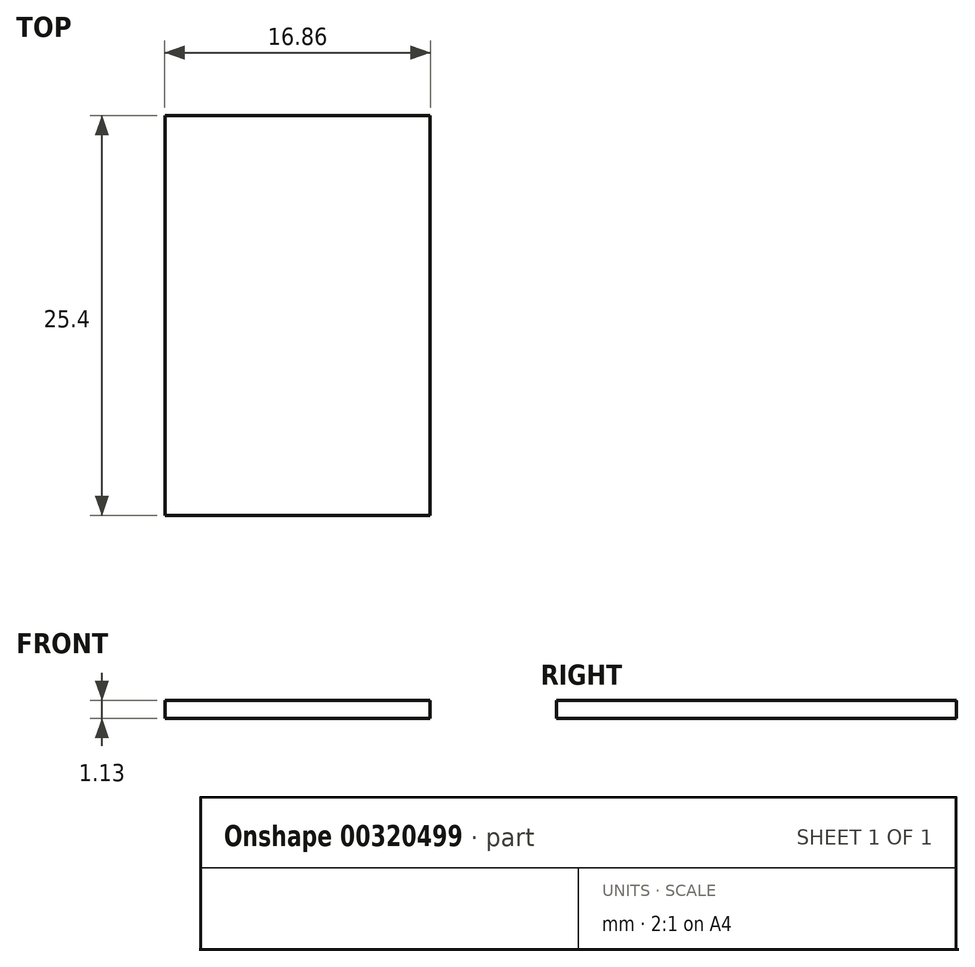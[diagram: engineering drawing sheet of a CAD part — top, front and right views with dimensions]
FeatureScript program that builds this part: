
annotation { "Feature Type Name" : "Feature", "Feature Type Description" : "" }
export const myFeature = defineFeature(function(context is Context, id is Id, definition is map)
    precondition{}
    {
        {
            var Q0;
            Q0=qCreatedBy(makeId("Front.planeOp"),FACE);
            var sketch = newSketch(context, id + "F0", { "sketchPlane" : qUnion([Q0])});
            skLineSegment(sketch, "E0.bottom", {"start": v(-22.85, 4.77) * mm, "end": v(-6, 4.77) * mm});
            skLineSegment(sketch, "E0.top", {"start": v(-22.85, 8.44) * mm, "end": v(-6, 8.44) * mm});
            skLineSegment(sketch, "E0.left", {"start": v(-22.85, 4.77) * mm, "end": v(-22.85, 8.44) * mm});
            skLineSegment(sketch, "E0.right", {"start": v(-6, 4.77) * mm, "end": v(-6, 8.44) * mm});
            skSolve(sketch);
        }
        {
            var Q0;
            Q0=makeQuery(id+"F0.imprint","IMPRINT",FACE,{"disambiguationData":[TD([[makeQuery(id+"F0.imprint","IMPRINT",EDGE,{"derivedFrom":sQuery(id+"F0.wireOp",EDGE,"E0.bottom")}),1.0]])]});
            extrude(context, id + "F1", {"entities" : qUnion([Q0]), "depth" : 25.4 * mm});
        }
        {
            var Q0;
            Q0=makeQuery(id+"F1.opExtrude","SWEPT_FACE",FACE,{"disambiguationData":[OSD([sQuery(id+"F0.wireOp",EDGE,"E0.bottom")])]});
            extrude(context, id + "F2", {"entities" : qUnion([Q0]), "operationType" : NewBodyOperationType.REMOVE, "oppositeDirection" : true, "depth" : 2.54 * mm});
        }
    });
